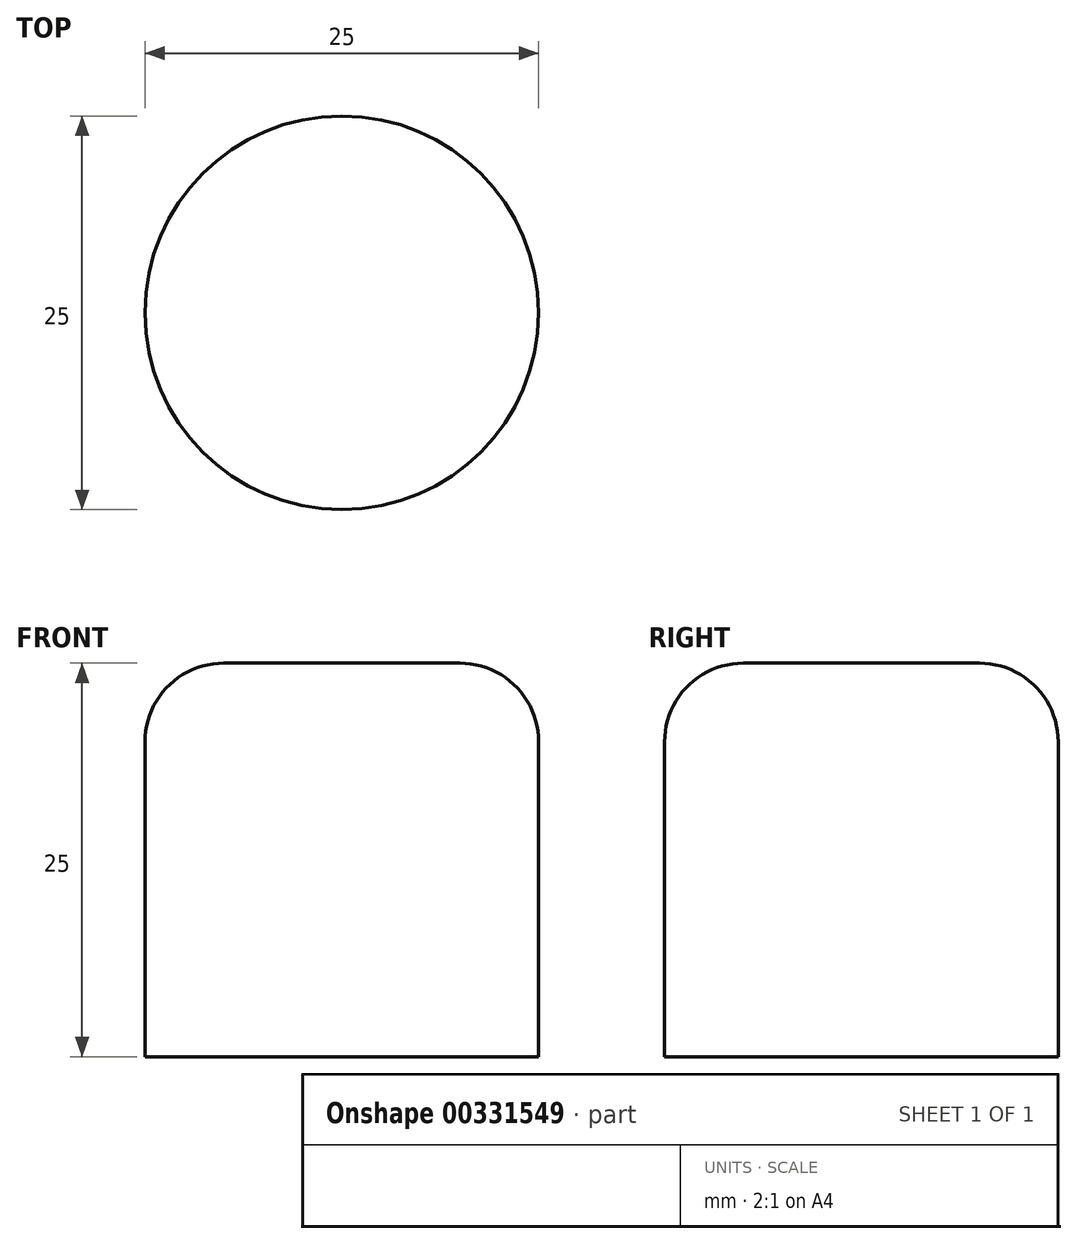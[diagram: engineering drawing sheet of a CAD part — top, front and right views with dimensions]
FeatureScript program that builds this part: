
annotation { "Feature Type Name" : "Feature", "Feature Type Description" : "" }
export const myFeature = defineFeature(function(context is Context, id is Id, definition is map)
    precondition{}
    {
        {
            var Q0;
            Q0=qCreatedBy(makeId("Top.planeOp"),FACE);
            var sketch = newSketch(context, id + "F0", { "sketchPlane" : qUnion([Q0])});
            skCircle(sketch, "E0", {"center": v(0, 0) * mm, "radius": 12.5 * mm});
            skSolve(sketch);
        }
        {
            var Q0;
            Q0=makeQuery(id+"F0.imprint","IMPRINT",FACE,{"disambiguationData":[TD([[makeQuery(id+"F0.imprint","IMPRINT",EDGE,{"derivedFrom":sQuery(id+"F0.wireOp",EDGE,"E0")}),1.0]])]});
            var Q1;
            Q1=sQuery(id+"F0.wireOp",EDGE,"E0");
            extrude(context, id + "F1", {"entities" : qUnion([Q0]), "surfaceEntities" : qUnion([Q1]), "depth" : 25 * mm, "offsetDistance" : 25 * mm});
        }
        {
            var Q0;
            Q0=makeQuery(id+"F1.opExtrude","CAP_FACE",FACE,{"disambiguationData":[OSD([sQuery(id+"F0.wireOp",EDGE,"E0")])],"isStart":false});
            fillet(context, id + "F2", {"entities" : qUnion([Q0]), "radius" : 5 * mm, "allowEdgeOverflow" : false});
        }
    });
